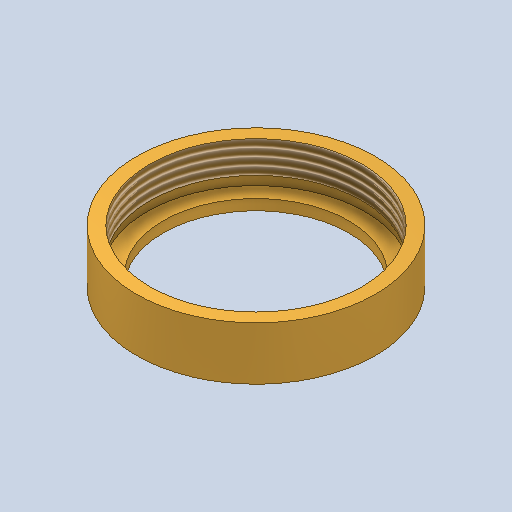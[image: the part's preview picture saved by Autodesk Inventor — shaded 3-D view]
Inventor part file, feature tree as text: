
AUTODESK INVENTOR PART (.ipt)
format: ipt  version: 2023 (Build 270158000, 158)  size: 158,720 bytes
history: native  units: mm
features: revolve x1, thread x1, sketch x1
ambient origin geometry x8: Origin, YZ Plane, XZ Plane, XY Plane, X Axis, Y Axis, Z Axis, Center Point
bodies: Solid1 (feature_tree)
feature tree (3):
  revolve  "Revolution1"  [1 undecoded]
  thread  "Thread1"  [1 undecoded]
  sketch  "Sketch1"  dims[d0=35.0mm d1=2.0mm d2=2.0mm d3=40.0mm d4=0.5mm d5=6.0mm d6=45.0mm d7=90.0deg d8=10.0mm d9=0.0mm]
note: 2 required parameter values undecoded (feature->parameter linkage not recoverable at this tier; creation-order binding heuristic only, values carry confidence <= 0.55)